# Revit family: Hager-Univers-IP65-D200-H550-Cl.II-encl-NoHosted-NL-en
name_source: partatom
category: Equipement électrique
units: mm (PartAtom-declared; Revit-internal decimal feet)

## family parameters
Basée sur le plan de construction = Oui
Configuration du panneau = Deux colonnes, circuits au sein
Cote de connecteur circulaire = Utiliser le diamètre
Couper avec des vides une fois chargée = Non
Partagée = Non
Point de calcul de pièce = Non
Toujours verticalement = Oui
Type d'élément = Tableau de raccordement

## types (1)
- Surface mounted (plaster) IP65 W300 H500 D200  - FL31S
    Commentaires du type = Univers
    EF000003 - Mounting method = EV000384 - Surface mounted (plaster)
    EF000007 - Colour = EV000270 - Grey
    EF000008 - Width = 300 mm  [stored 0.984252 ft]
    EF000040 - Height = 500 mm  [stored 1.64042 ft]
    EF000049 - Depth = 200 mm  [stored 0.656168 ft]
    EF000116 - RAL-number = 7035
    EF000118 - With mounting plate = Non
    EF000218 - Built-in depth = 0 mm  [stored 0 ft]
    EF000266 - Number of rows = 3
    EF000339 - Type of cover = EV004216 - Door
    EF000437 - Number of conduit inlets = 0
    EF001088 - Extension possible = Oui
    EF001131 - Internal depth = 150 mm  [stored 0.492126 ft]
    EF001596 - Material housing = EV000139 - Plastic
    EF001613 - Circuit integrity = EV000494 - None
    EF002950 - Width in number of modular spacings = 12
    EF003532 - Suitable for outdoor use = Oui
    EF004293 - Impact strength = EV008784 - IK10
    EF004427 - Number of modules = 36
    EF004464 - Type of door = EV002646 - Single
    EF005474 - Degree of protection (IP) = EV006421 - IP65
    EF006244 - Transparent cover/door = Non
    EF006306 - With lock = Oui
    EF007800 - Suitable for lightning protection = Oui
    EF008873 - Nominal current (In) = 630 A
    EF009170 - Material plate thickness cabinet = 1 mm  [stored 0.00328084 ft]
    EF009171 - Material plate thickness door/cover = 2 mm  [stored 0.00656168 ft]
    EF009212 - Cover model = EV000116 - Closed
    EF009554 - Number of openings for flange plates = 0
    EF015940 - Cover with overpressure release = Non
    Elévation par défaut = 1219 mm
    Fabricant = Hager
    HG000002 - With door or cover = Oui
    HG000003 - Range = Univers
    HG000004 - Manufacturer reference = FL31S
    HG000006 - Flush mounted = Non
    HG000009 - Double swing door = Non
    HG000010 - Asymmetric doors = Non
    HG000023 - Double section enclosure = Non
    HG000024 - Bottom section height = 600 mm
    HG000026 - Floor standing = Non
    HG000027 - Plinth height = 0 mm  [stored 0 ft]

note: [stored X ft] marks values corroborated as IEEE doubles in the binary element streams (Revit-internal decimal feet)

## geometry (parser evidence)
native form markers: Blend x4, Sweep x5
no freeform markers — native parametric forms only
